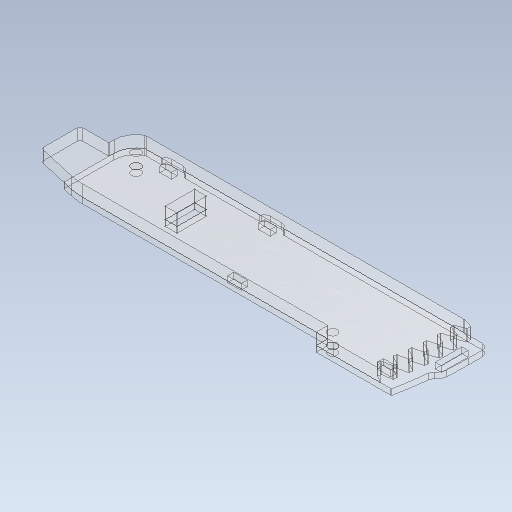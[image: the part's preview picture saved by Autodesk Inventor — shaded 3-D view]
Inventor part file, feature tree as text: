
AUTODESK INVENTOR PART (.ipt)
format: ipt  version: 2021 (Build 250183000, 183)  size: 372,736 bytes
history: native  units: mm
features: other x5, sketch x2
ambient origin geometry x8: Origin, YZ Plane, XZ Plane, XY Plane, X Axis, Y Axis, Z Axis, Center Point
bodies: Solid1 (feature_tree), Solid2 (feature_tree), Solid3 (feature_tree)
feature tree (7):
  other  "Laser-Slot-Side.ipt"
  other  "Solid1::Laser-Slot-Side.ipt"
  other  "TaggingFeature1"
  sketch  "Sketch1"  dims[d0=10.0mm]
  sketch  "Sketch3"
  other  "Gear-4mm::Laser-Slot-Side.ipt"
  other  "Plate-2mm::Laser-Slot-Side.ipt"
